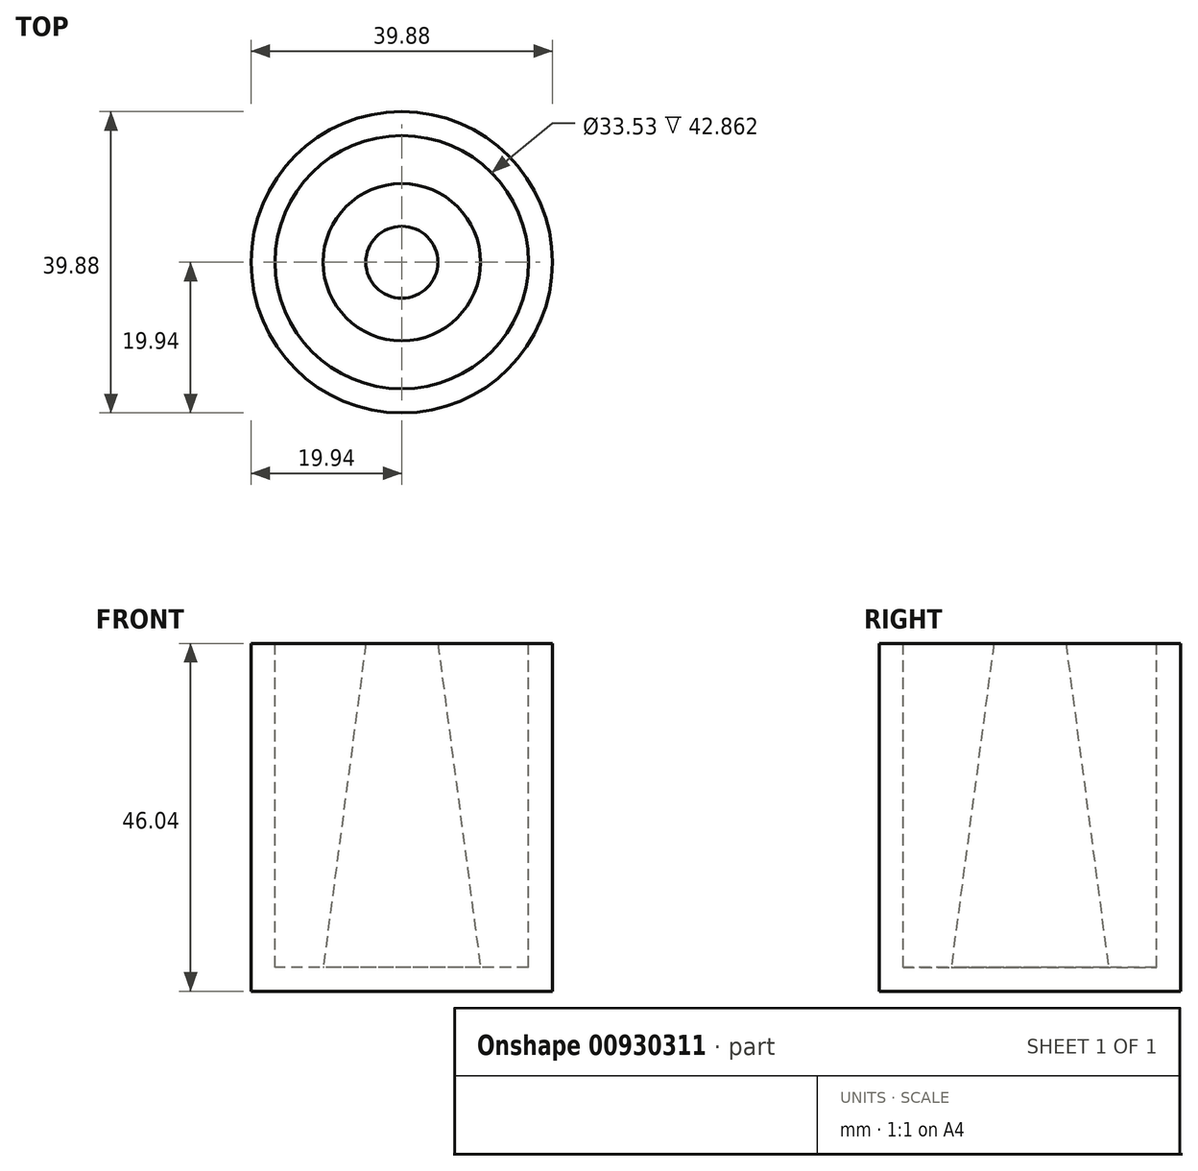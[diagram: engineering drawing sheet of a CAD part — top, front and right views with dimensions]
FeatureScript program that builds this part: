
annotation { "Feature Type Name" : "Feature", "Feature Type Description" : "" }
export const myFeature = defineFeature(function(context is Context, id is Id, definition is map)
    precondition{}
    {
        {
            var Q0;
            Q0=qCreatedBy(makeId("Front.planeOp"),FACE);
            var sketch = newSketch(context, id + "F0", { "sketchPlane" : qUnion([Q0])});
            skLineSegment(sketch, "E0", {"start": v(0, 12.7) * mm, "end": v(0, 7.94) * mm});
            skLineSegment(sketch, "E1", {"start": v(0, 50.8) * mm, "end": v(0, 7.94) * mm});
            skPoint(sketch, "E2.end.orphan", {"position": v(12.13, 25.4) * mm});
            skLineSegment(sketch, "E3", {"start": v(10.4, 7.94) * mm, "end": v(16.61, 7.94) * mm});
            skLineSegment(sketch, "E4", {"start": v(0, 50.8) * mm, "end": v(4.76, 50.8) * mm});
            skLineSegment(sketch, "E5", {"start": v(9.78, 12.7) * mm, "end": v(4.76, 50.8) * mm});
            skLineSegment(sketch, "E6", {"start": v(16.76, 50.8) * mm, "end": v(16.76, 13.3) * mm});
            skLineSegment(sketch, "E7", {"start": v(16.76, 13.3) * mm, "end": v(16.76, 7.94) * mm});
            skLineSegment(sketch, "E8", {"start": v(9.78, 12.7) * mm, "end": v(10.4, 7.94) * mm});
            skLineSegment(sketch, "E9", {"start": v(16.76, 50.8) * mm, "end": v(19.94, 50.8) * mm});
            skLineSegment(sketch, "E10", {"start": v(19.94, 50.8) * mm, "end": v(19.94, 4.76) * mm});
            skLineSegment(sketch, "E11", {"start": v(0, 7.94) * mm, "end": v(0, 4.76) * mm});
            skLineSegment(sketch, "E12", {"start": v(0, 4.76) * mm, "end": v(19.94, 4.76) * mm});
            skLineSegment(sketch, "E13.trimOffspring", {"start": v(10.4, 7.94) * mm, "end": v(16.76, 7.94) * mm});
            skSolve(sketch);
        }
        {
            var Q0;
            Q0 = qSketchRegion(id + "F0", true);
            var Q1;
            Q1=sQuery(id+"F0.wireOp",EDGE,"E1");
            revolve(context, id + "F1", {"surfaceOperationType" : NewSurfaceOperationType.NEW, "entities" : qUnion([Q0]), "axis" : qUnion([Q1]), "revolveType" : RevolveType.FULL});
        }
        {
            var Q0;
            Q0=makeQuery(id+"F1.opRevolve","SWEPT_FACE",FACE,{"disambiguationData":[OSD([sQuery(id+"F0.wireOp",EDGE,"E9")])]});
            var sketch = newSketch(context, id + "F2", { "sketchPlane" : qUnion([Q0])});
            skLineSegment(sketch, "E14", {"start": v(0, -19.94) * mm, "end": v(0, -16.76) * mm});
            skLineSegment(sketch, "E15", {"start": v(0, -19.94) * mm, "end": v(26.64, -19.94) * mm});
            skSolve(sketch);
        }
        {
            var Q0;
            Q0=makeQuery(id+"F1.opRevolve","SWEPT_FACE",FACE,{"disambiguationData":[OSD([sQuery(id+"F0.wireOp",EDGE,"E12")])]});
            var sketch = newSketch(context, id + "F3", { "sketchPlane" : qUnion([Q0])});
            skLineSegment(sketch, "E16", {"start": v(0, 19.94) * mm, "end": v(0, 0) * mm});
            skSolve(sketch);
        }
        {
            var Q0;
            Q0=sQuery(id+"F2.wireOp",VERTEX,"E14.start");
            var Q1;
            Q1=sQuery(id+"F2.wireOp",VERTEX,"E15.end");
            var Q2;
            Q2=sQuery(id+"F3.wireOp",VERTEX,"E16.start");
            cPlane(context, id + "F4", {"entities" : qUnion([Q0, Q1, Q2]), "cplaneType" : CPlaneType.THREE_POINT, "offset" : 0 * mm, "width" : 152.4 * mm, "height" : 152.4 * mm});
        }
    });
